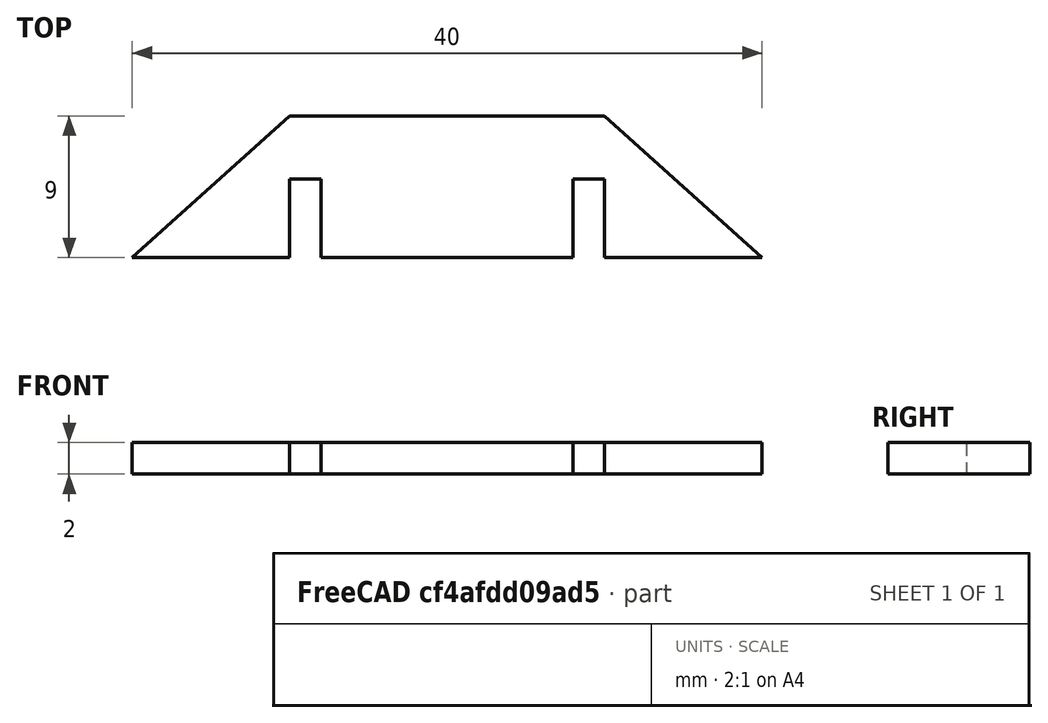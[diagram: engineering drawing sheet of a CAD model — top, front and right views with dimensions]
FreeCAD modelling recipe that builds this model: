
FCSTD DOCUMENT  (FreeCAD 0.14R3700 (Git))
Label: BIRR_fixPile
License: CC-BY 3.0
LicenseURL: http://creativecommons.org/licenses/by/3.0/
objects: Sketcher::SketchObject×1, Part::Extrusion×1, Part::Feature×1
note: 3 computed .brp shape members not serialized (recipe doc carries the construction recipe); baked Part::Feature solids carry a one-line shape summary decoded from their .brp

FEATURE [Sketcher::SketchObject] Sketch  label="fixPile"
  sketch-geometry (12):
    g0: LineSegment StartX=40 StartY=0 StartZ=0 EndX=30 EndY=0 EndZ=0
    g1: LineSegment StartX=30 StartY=0 StartZ=0 EndX=30 EndY=5 EndZ=0
    g2: LineSegment StartX=10 StartY=5 StartZ=0 EndX=10 EndY=0 EndZ=0
    g3: LineSegment StartX=10 StartY=0 StartZ=0 EndX=0 EndY=0 EndZ=0
    g4: LineSegment StartX=12 StartY=0 StartZ=0 EndX=28 EndY=0 EndZ=0
    g5: LineSegment StartX=28 StartY=0 StartZ=0 EndX=28 EndY=5 EndZ=0
    g6: LineSegment StartX=28 StartY=5 StartZ=0 EndX=30 EndY=5 EndZ=0
    g7: LineSegment StartX=12 StartY=0 StartZ=0 EndX=12 EndY=5 EndZ=0
    g8: LineSegment StartX=12 StartY=5 StartZ=0 EndX=10 EndY=5 EndZ=0
    g9: LineSegment StartX=40 StartY=0 StartZ=0 EndX=30 EndY=9 EndZ=0
    g10: LineSegment StartX=0 StartY=0 StartZ=0 EndX=10 EndY=9 EndZ=0
    g11: LineSegment StartX=10 StartY=9 StartZ=0 EndX=30 EndY=9 EndZ=0
  constraints (35):
    c: Horizontal(g0)
    c: Coincident(g1,g0)
    c: Vertical(g1)
    c: Vertical(g2)
    c: Coincident(g3,g2)
    c: Horizontal(g3)
    c: Horizontal(g4)
    c: Coincident(g5,g4)
    c: Vertical(g5)
    c: Coincident(g6,g5)
    c: Horizontal(g6)
    c: Coincident(g7,g4)
    c: Vertical(g7)
    c: Coincident(g8,g7)
    c: Coincident(g8,g2)
    c: DistanceX(g8) = -2
    c: Coincident(g6,g1)
    c: DistanceX(g6) = 2
    c: DistanceX(g2,g1) = 20
    c: PointOnObject(g0,g4)
    c: PointOnObject(g2,g4)
    c: DistanceY(g-1,g2) = 5
    c: Horizontal(g8)
    c: PointOnObject(g5,g8)
    c: DistanceX(g3,g2) = 10
    c: DistanceX(g0) = -10
    c: Coincident(g3,g-1)
    c: Coincident(g11,g10)
    c: Coincident(g11,g9)
    c: Horizontal(g11)
    c: PointOnObject(g10,g2)
    c: PointOnObject(g9,g1)
    c: DistanceY(g9,g1) = -4
    c: Coincident(g10,g-1)
    c: Coincident(g9,g0)
FEATURE [Part::Extrusion] Extrude
  Base = -> Sketch
  Dir = (0,0,2)
  Solid = true
FEATURE [Part::Feature] Extrude001  label="fixPile_copy"
  shape: bbox 40 x 9 x 2 mm, 14 faces (baked)
